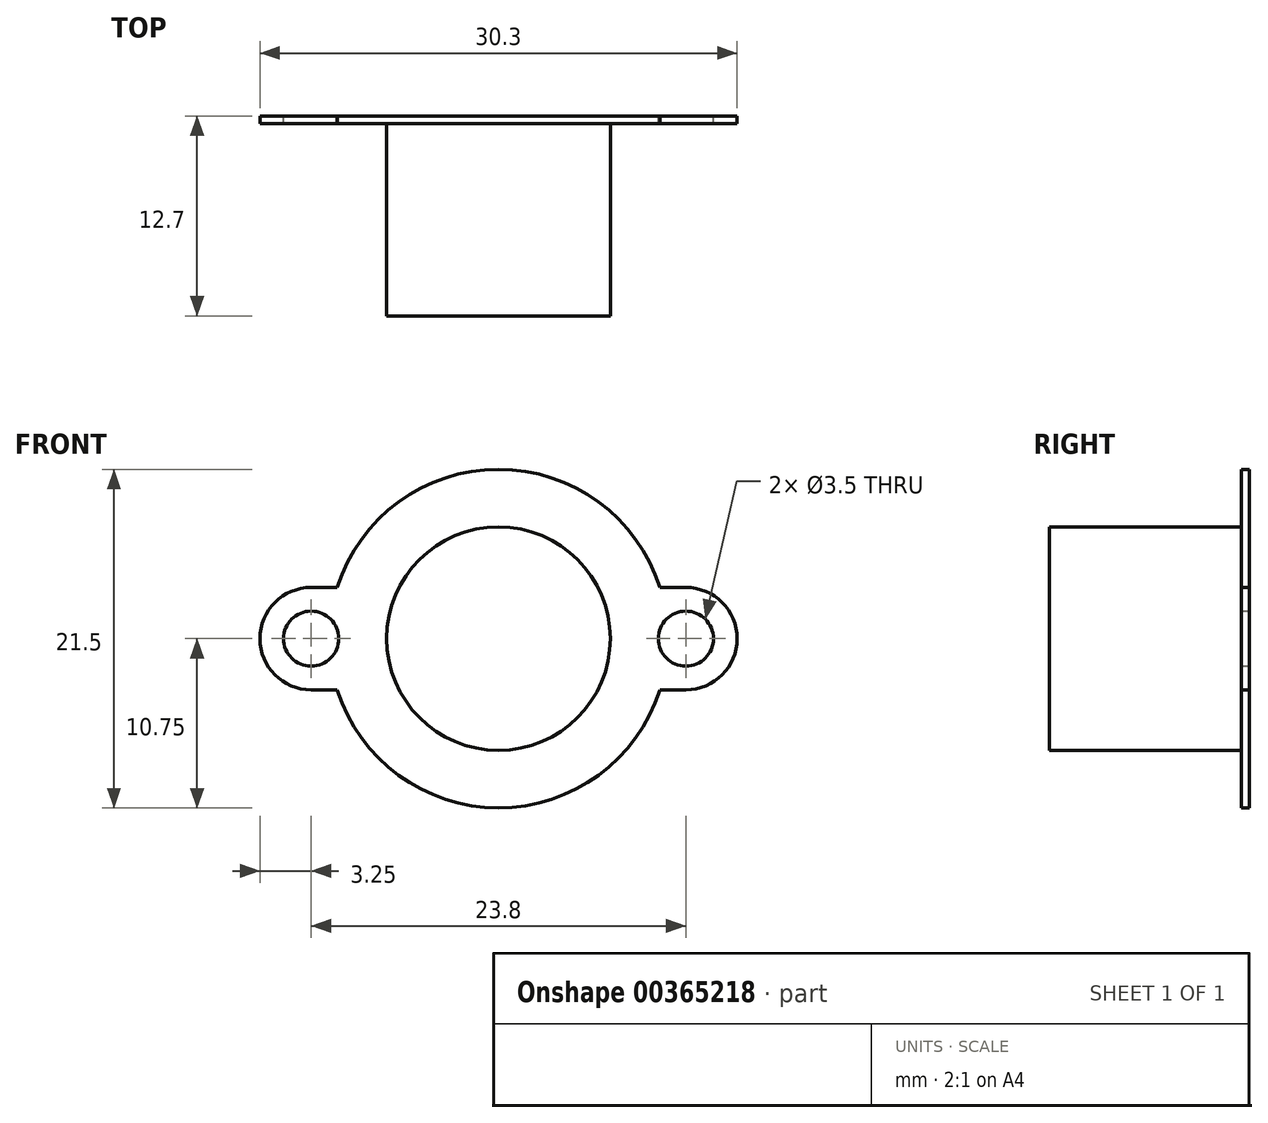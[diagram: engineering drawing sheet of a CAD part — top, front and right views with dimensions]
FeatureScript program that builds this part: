
annotation { "Feature Type Name" : "Feature", "Feature Type Description" : "" }
export const myFeature = defineFeature(function(context is Context, id is Id, definition is map)
    precondition{}
    {
        {
            var Q0;
            Q0=qCreatedBy(makeId("Front.planeOp"),FACE);
            var sketch = newSketch(context, id + "F0", { "sketchPlane" : qUnion([Q0])});
            skCircle(sketch, "E0", {"center": v(0, 0) * mm, "radius": 7.1 * mm});
            skSolve(sketch);
        }
        {
            var Q0;
            Q0 = qSketchRegion(id + "F0", true);
            extrude(context, id + "F1", {"entities" : qUnion([Q0]), "depth" : 12.7 * mm});
        }
        {
            var Q0;
            Q0=qCreatedBy(makeId("Front.planeOp"),FACE);
            var sketch = newSketch(context, id + "F2", { "sketchPlane" : qUnion([Q0])});
            skLineSegment(sketch, "E1", {"start": v(0, 0) * mm, "end": v(11.9, 0) * mm, "construction": true});
            skCircle(sketch, "E2", {"center": v(11.9, 0) * mm, "radius": 1.75 * mm});
            skLineSegment(sketch, "E3", {"start": v(11.9, -3.25) * mm, "end": v(10.25, -3.25) * mm});
            skLineSegment(sketch, "E4", {"start": v(11.9, 3.25) * mm, "end": v(10.25, 3.25) * mm});
            skArc(sketch, "E5", {"start": v(0, 10.75) * mm, "mid": v(6.35, 8.67) * mm, "end": v(10.25, 3.25) * mm});
            skArc(sketch, "E6", {"start": v(11.9, 3.25) * mm, "mid": v(15.15, 0) * mm, "end": v(11.9, -3.25) * mm});
            skArc(sketch, "E7", {"start": v(10.25, -3.25) * mm, "mid": v(6.35, -8.67) * mm, "end": v(0, -10.75) * mm});
            skLineSegment(sketch, "E8.MirrorCS", {"start": v(-11.9, 3.25) * mm, "end": v(-10.25, 3.25) * mm});
            skArc(sketch, "E9.MirrorCS", {"start": v(0, 10.75) * mm, "mid": v(-6.35, 8.67) * mm, "end": v(-10.25, 3.25) * mm});
            skArc(sketch, "E10.MirrorCS", {"start": v(-11.9, 3.25) * mm, "mid": v(-15.15, 0) * mm, "end": v(-11.9, -3.25) * mm});
            skLineSegment(sketch, "E11.MirrorCS", {"start": v(-11.9, -3.25) * mm, "end": v(-10.25, -3.25) * mm});
            skArc(sketch, "E12.MirrorCS", {"start": v(-10.25, -3.25) * mm, "mid": v(-6.35, -8.67) * mm, "end": v(0, -10.75) * mm});
            skCircle(sketch, "E13.MirrorC", {"center": v(-11.9, 0) * mm, "radius": 1.75 * mm});
            skSolve(sketch);
        }
        {
            var Q0;
            Q0 = qSketchRegion(id + "F2", true);
            extrude(context, id + "F3", {"entities" : qUnion([Q0]), "operationType" : NewBodyOperationType.ADD, "depth" : .5 * mm});
        }
    });
